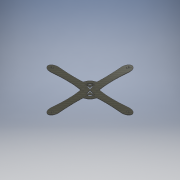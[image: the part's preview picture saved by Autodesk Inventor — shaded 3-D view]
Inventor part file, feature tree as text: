
AUTODESK INVENTOR PART (.ipt)
format: ipt  version: 2017 (Build 210142000, 142)  size: 449,024 bytes
history: native  units: mm
features: other x8, extrude x8, sketch x7, reference x4, projected_geometry x1
ambient origin geometry x8: Origin, YZ Plane, XZ Plane, XY Plane, X Axis, Y Axis, Z Axis, Center Point
bodies: Body1 (feature_tree)
feature tree (28):
  other  "Bryła1"
  extrude  "Wyciągnięcie proste1"  Depth=15.0mm
  sketch  "Szkic2"
  extrude  "Wyciągnięcie proste2"  Depth=225.0mm
  extrude  "Wyciągnięcie proste3"  Depth=8.0mm
  other  "Pogrubienie1"
  extrude  "Wyciągnięcie proste4"  Depth=80.0mm
  extrude  "Wyciągnięcie proste5"  Depth=80.0mm
  extrude  "Wyciągnięcie proste6"  Depth=15.0mm
  extrude  "Wyciągnięcie proste7"  Depth=30.0mm
  extrude  "Wyciągnięcie proste8"  Depth=30.0mm
  other  "Pogrubienie2"
  sketch  "Szkic1"
  projected_geometry  "Pętla rzutowana1"
  sketch  "Szkic3"
  reference  "Odniesienie1"
  reference  "Odniesienie2"
  reference  "Odniesienie3"
  reference  "Odniesienie4"
  sketch  "Szkic4"
  sketch  "Szkic5"
  sketch  "Szkic6"
  sketch  "Szkic7"
  other  "Zespół1"
  other  "rurka_fi5_rama_rama_lipol_MIR_MIR:1"
  other  "rurka_fi5_rama_rama_lipol_MIR1:1"
  other  "rurka_fi5_rama_rama_lipol:4"
  other  "rurka_fi5_rama_rama_lipol_MIR:1"
